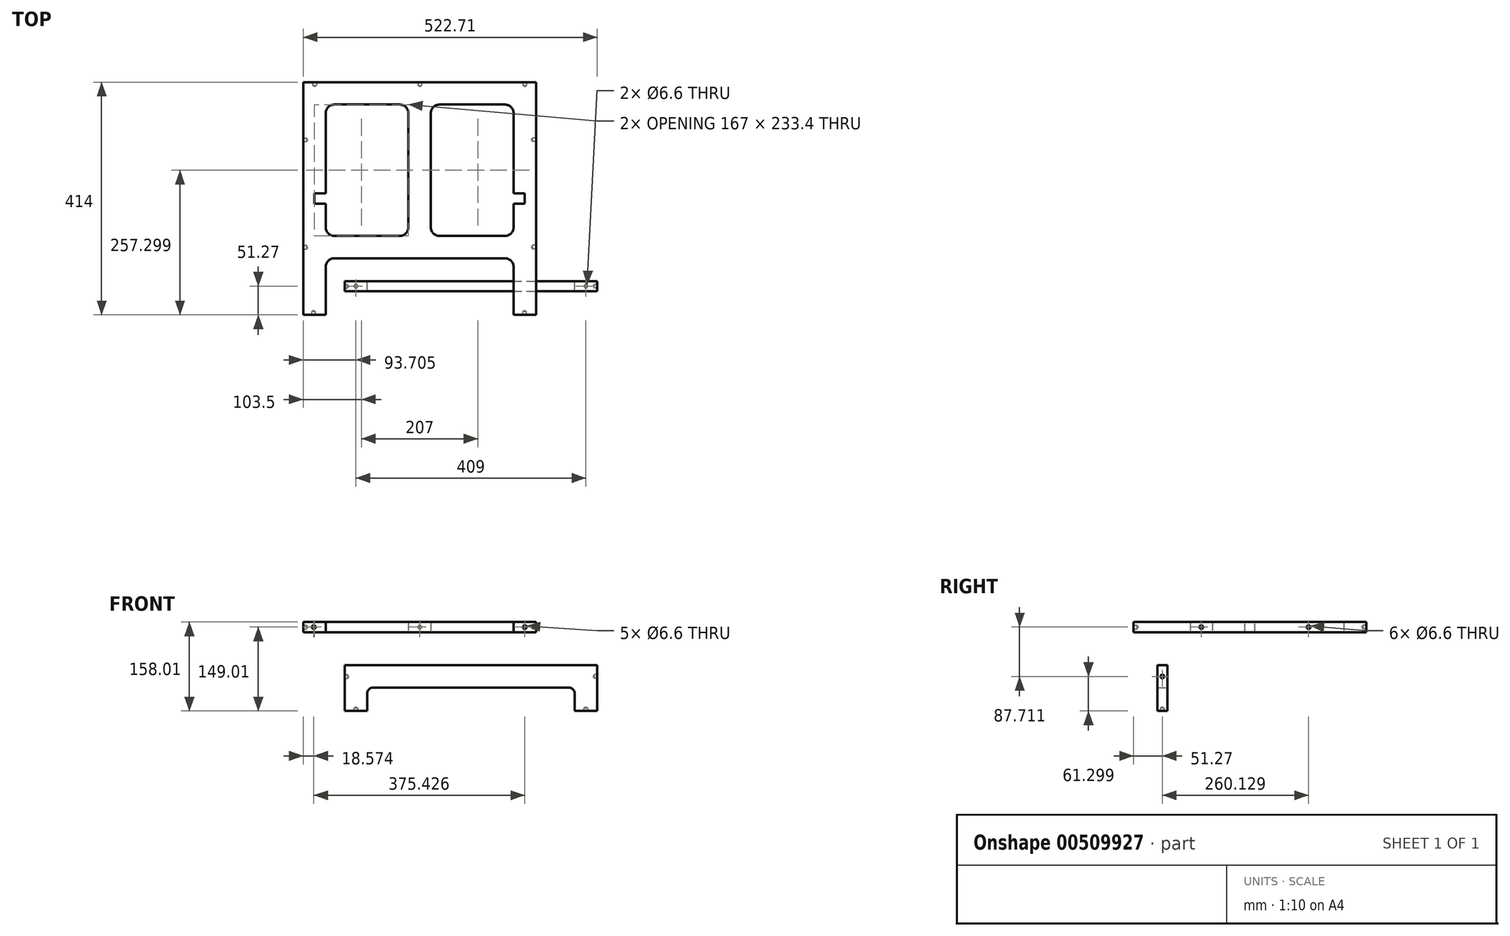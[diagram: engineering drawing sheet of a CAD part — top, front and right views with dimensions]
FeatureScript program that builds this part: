
annotation { "Feature Type Name" : "Feature", "Feature Type Description" : "" }
export const myFeature = defineFeature(function(context is Context, id is Id, definition is map)
    precondition{}
    {
        {
            var Q0;
            Q0=qCreatedBy(makeId("Top.planeOp"),FACE);
            var sketch = newSketch(context, id + "F0", { "sketchPlane" : qUnion([Q0])});
            skLineSegment(sketch, "E0.top", {"start": v(-192, 353.73) * mm, "end": v(222, 353.73) * mm});
            skLineSegment(sketch, "E0.left", {"start": v(-192, -60.27) * mm, "end": v(-192, 353.73) * mm});
            skLineSegment(sketch, "E0.right", {"start": v(222, -60.27) * mm, "end": v(222, 353.73) * mm});
            skLineSegment(sketch, "E1.top", {"start": v(-137, 40.33) * mm, "end": v(167, 40.33) * mm});
            skLineSegment(sketch, "E1.left", {"start": v(-152, -60.27) * mm, "end": v(-152, 25.33) * mm});
            skLineSegment(sketch, "E1.right", {"start": v(182, -60.27) * mm, "end": v(182, 25.33) * mm});
            skLineSegment(sketch, "E2.bottom", {"start": v(50, 313.73) * mm, "end": v(167, 313.73) * mm});
            skLineSegment(sketch, "E2.top", {"start": v(50, 80.33) * mm, "end": v(167, 80.33) * mm});
            skLineSegment(sketch, "E2.left", {"start": v(35, 298.73) * mm, "end": v(35, 95.33) * mm});
            skLineSegment(sketch, "E2.right", {"start": v(182, 298.73) * mm, "end": v(182, 95.33) * mm});
            skPoint(sketch, "E3.visualSharp", {"position": v(-157, 313.73) * mm});
            skPoint(sketch, "E4.visualSharp", {"position": v(0, 80.33) * mm});
            skPoint(sketch, "E5.visualSharp", {"position": v(-152, 98.33) * mm});
            skPoint(sketch, "E6.visualSharp", {"position": v(35, 313.73) * mm});
            skArc(sketch, "E6.filletArc", {"start": v(50, 313.73) * mm, "mid": v(39.4, 309.34) * mm, "end": v(35, 298.73) * mm});
            skPoint(sketch, "E7.visualSharp", {"position": v(182, 313.73) * mm});
            skArc(sketch, "E7.filletArc", {"start": v(182, 298.73) * mm, "mid": v(177.6, 309.34) * mm, "end": v(167, 313.73) * mm});
            skPoint(sketch, "E8.visualSharp", {"position": v(182, 80.33) * mm});
            skArc(sketch, "E8.filletArc", {"start": v(167, 80.33) * mm, "mid": v(177.6, 84.72) * mm, "end": v(182, 95.33) * mm});
            skPoint(sketch, "E9.visualSharp", {"position": v(35, 80.33) * mm});
            skArc(sketch, "E9.filletArc", {"start": v(35, 95.33) * mm, "mid": v(39.4, 84.72) * mm, "end": v(50, 80.33) * mm});
            skPoint(sketch, "E10.visualSharp", {"position": v(-152, 40.33) * mm});
            skArc(sketch, "E10.filletArc", {"start": v(-137, 40.33) * mm, "mid": v(-147.6, 35.94) * mm, "end": v(-152, 25.33) * mm});
            skPoint(sketch, "E11.visualSharp", {"position": v(182, 40.33) * mm});
            skArc(sketch, "E11.filletArc", {"start": v(182, 25.33) * mm, "mid": v(177.6, 35.94) * mm, "end": v(167, 40.33) * mm});
            skLineSegment(sketch, "E12", {"start": v(-192, -60.27) * mm, "end": v(-152, -60.27) * mm});
            skLineSegment(sketch, "E13", {"start": v(182, -60.27) * mm, "end": v(222, -60.27) * mm});
            skLineSegment(sketch, "E14", {"start": v(15, 353.73) * mm, "end": v(15, -60.27) * mm});
            skLineSegment(sketch, "E15.MirrorCS", {"start": v(-5, 298.73) * mm, "end": v(-5, 95.33) * mm});
            skArc(sketch, "E16.MirrorCS", {"start": v(-20, 313.73) * mm, "mid": v(-9.4, 309.34) * mm, "end": v(-5, 298.73) * mm});
            skLineSegment(sketch, "E17.MirrorCS", {"start": v(-20, 313.73) * mm, "end": v(-137, 313.73) * mm});
            skArc(sketch, "E18.MirrorCS", {"start": v(-152, 298.73) * mm, "mid": v(-147.6, 309.34) * mm, "end": v(-137, 313.73) * mm});
            skLineSegment(sketch, "E19.MirrorCS", {"start": v(-152, 298.73) * mm, "end": v(-152, 95.33) * mm});
            skArc(sketch, "E20.MirrorCS", {"start": v(-137, 80.33) * mm, "mid": v(-147.6, 84.72) * mm, "end": v(-152, 95.33) * mm});
            skLineSegment(sketch, "E21.MirrorCS", {"start": v(-20, 80.33) * mm, "end": v(-137, 80.33) * mm});
            skArc(sketch, "E22.MirrorCS", {"start": v(-5, 95.33) * mm, "mid": v(-9.4, 84.72) * mm, "end": v(-20, 80.33) * mm});
            skSolve(sketch);
        }
        {
            var Q0;
            Q0=makeQuery(id+"F0.imprint","IMPRINT",FACE,{"disambiguationData":[TD([[makeQuery(id+"F0.imprint","IMPRINT",EDGE,{"derivedFrom":sQuery(id+"F0.wireOp",EDGE,"E0.top")}),-1.0]])]});
            extrude(context, id + "F1", {"entities" : qUnion([Q0]), "depth" : 18 * mm, "offsetDistance" : 25 * mm});
        }
        {
            var Q0;
            Q0=makeQuery(id+"F1.opExtrude","SWEPT_FACE",FACE,{"disambiguationData":[OSD([sQuery(id+"F0.wireOp",EDGE,"E0.top")])]});
            var sketch = newSketch(context, id + "F2", { "sketchPlane" : qUnion([Q0])});
            skLineSegment(sketch, "E23", {"start": v(-222, 9) * mm, "end": v(192, 9) * mm});
            skPoint(sketch, "E24", {"position": v(-202, 9) * mm});
            skPoint(sketch, "E25", {"position": v(-15, 9) * mm});
            skPoint(sketch, "E26", {"position": v(172, 9) * mm});
            skSolve(sketch);
        }
        {
            var Q0;
            Q0=makeQuery(id+"F1.opExtrude","SWEPT_FACE",FACE,{"disambiguationData":[OSD([sQuery(id+"F0.wireOp",EDGE,"E13")])]});
            var sketch = newSketch(context, id + "F3", { "sketchPlane" : qUnion([Q0])});
            skLineSegment(sketch, "E27", {"start": v(222, 9) * mm, "end": v(-191.48, 9) * mm});
            skPoint(sketch, "E28", {"position": v(202, 9) * mm});
            skPoint(sketch, "E29", {"position": v(-173.43, 9) * mm});
            skSolve(sketch);
        }
        {
            var Q0;
            Q0=makeQuery(id+"F1.opExtrude","SWEPT_FACE",FACE,{"disambiguationData":[OSD([sQuery(id+"F0.wireOp",EDGE,"E0.right")])]});
            var sketch = newSketch(context, id + "F4", { "sketchPlane" : qUnion([Q0])});
            skLineSegment(sketch, "E30", {"start": v(-60.27, 9) * mm, "end": v(353.73, 9) * mm});
            skPoint(sketch, "E31", {"position": v(60.33, 9) * mm});
            skPoint(sketch, "E32", {"position": v(251.13, 9) * mm});
            skSolve(sketch);
        }
        {
            var Q0;
            Q0=makeQuery(id+"F1.opExtrude","SWEPT_FACE",FACE,{"disambiguationData":[OSD([sQuery(id+"F0.wireOp",EDGE,"E0.left")])]});
            var sketch = newSketch(context, id + "F5", { "sketchPlane" : qUnion([Q0])});
            skLineSegment(sketch, "E33", {"start": v(60.27, 9) * mm, "end": v(-353.73, 9) * mm});
            skPoint(sketch, "E34", {"position": v(-60.33, 9) * mm});
            skPoint(sketch, "E35", {"position": v(-251.13, 9) * mm});
            skSolve(sketch);
        }
        {
            var Q0;
            Q0=sQuery(id+"F3.wireOp",VERTEX,"E28");
            var Q1;
            Q1=sQuery(id+"F3.wireOp",VERTEX,"E29");
            var Q2;
            Q2=sQuery(id+"F5.wireOp",VERTEX,"E34");
            var Q3;
            Q3=sQuery(id+"F5.wireOp",VERTEX,"E35");
            var Q4;
            Q4=sQuery(id+"F2.wireOp",VERTEX,"E26");
            var Q5;
            Q5=sQuery(id+"F2.wireOp",VERTEX,"E25");
            var Q6;
            Q6=sQuery(id+"F2.wireOp",VERTEX,"E24");
            var Q7;
            Q7=sQuery(id+"F4.wireOp",VERTEX,"E31");
            var Q8;
            Q8=sQuery(id+"F4.wireOp",VERTEX,"E32");
            var Q9;
            Q9=makeQuery(id+"F1.opExtrude","SWEPT_BODY",BODY,{"disambiguationData":[OSD([sQuery(id+"F0.wireOp",EDGE,"E0.top"),sQuery(id+"F0.wireOp",EDGE,"E0.left"),sQuery(id+"F0.wireOp",EDGE,"E0.right"),sQuery(id+"F0.wireOp",EDGE,"E1.top"),sQuery(id+"F0.wireOp",EDGE,"E1.left"),sQuery(id+"F0.wireOp",EDGE,"E1.right"),sQuery(id+"F0.wireOp",EDGE,"E2.bottom"),sQuery(id+"F0.wireOp",EDGE,"E2.top"),sQuery(id+"F0.wireOp",EDGE,"E2.left"),sQuery(id+"F0.wireOp",EDGE,"E2.right"),sQuery(id+"F0.wireOp",EDGE,"E6.filletArc"),sQuery(id+"F0.wireOp",EDGE,"E7.filletArc"),sQuery(id+"F0.wireOp",EDGE,"E8.filletArc"),sQuery(id+"F0.wireOp",EDGE,"E9.filletArc"),sQuery(id+"F0.wireOp",EDGE,"E10.filletArc"),sQuery(id+"F0.wireOp",EDGE,"E11.filletArc"),sQuery(id+"F0.wireOp",EDGE,"E12"),sQuery(id+"F0.wireOp",EDGE,"E13"),sQuery(id+"F0.wireOp",EDGE,"E15.MirrorCS"),sQuery(id+"F0.wireOp",EDGE,"E16.MirrorCS"),sQuery(id+"F0.wireOp",EDGE,"E17.MirrorCS"),sQuery(id+"F0.wireOp",EDGE,"E18.MirrorCS"),sQuery(id+"F0.wireOp",EDGE,"E19.MirrorCS"),sQuery(id+"F0.wireOp",EDGE,"E20.MirrorCS"),sQuery(id+"F0.wireOp",EDGE,"E21.MirrorCS"),sQuery(id+"F0.wireOp",EDGE,"E22.MirrorCS")])]});
            hole(context, id + "F6", {"style" : HoleStyle.SIMPLE, "endStyle" : HoleEndStyle.BLIND, "standardTappedOrClearance" : lookupTablePath({ "standard" : "ISO", "fit" : "Normal", "size" : "M6", "type" : "Clearance" }), "standardBlindInLast" : lookupTablePath({ "fit" : "Standard", "standard" : "ISO", "size" : "M6", "type" : "Clearance" }), "holeDiameter" : 6.6 * mm, "holeDepth" : 6 * mm, "isTappedThrough" : true, "tappedDepth" : 12 * mm, "tapClearance" : 3, "locations" : qUnion([Q0, Q1, Q2, Q3, Q4, Q5, Q6, Q7, Q8]), "scope" : qUnion([Q9])});
        }
        {
            var Q0;
            Q0=makeQuery(id+"F1.opExtrude","SWEPT_BODY",BODY,{"disambiguationData":[OSD([sQuery(id+"F0.wireOp",EDGE,"E0.top"),sQuery(id+"F0.wireOp",EDGE,"E0.left"),sQuery(id+"F0.wireOp",EDGE,"E0.right"),sQuery(id+"F0.wireOp",EDGE,"E1.top"),sQuery(id+"F0.wireOp",EDGE,"E1.left"),sQuery(id+"F0.wireOp",EDGE,"E1.right"),sQuery(id+"F0.wireOp",EDGE,"E2.bottom"),sQuery(id+"F0.wireOp",EDGE,"E2.top"),sQuery(id+"F0.wireOp",EDGE,"E2.left"),sQuery(id+"F0.wireOp",EDGE,"E2.right"),sQuery(id+"F0.wireOp",EDGE,"E6.filletArc"),sQuery(id+"F0.wireOp",EDGE,"E7.filletArc"),sQuery(id+"F0.wireOp",EDGE,"E8.filletArc"),sQuery(id+"F0.wireOp",EDGE,"E9.filletArc"),sQuery(id+"F0.wireOp",EDGE,"E10.filletArc"),sQuery(id+"F0.wireOp",EDGE,"E11.filletArc"),sQuery(id+"F0.wireOp",EDGE,"E12"),sQuery(id+"F0.wireOp",EDGE,"E13"),sQuery(id+"F0.wireOp",EDGE,"E15.MirrorCS"),sQuery(id+"F0.wireOp",EDGE,"E16.MirrorCS"),sQuery(id+"F0.wireOp",EDGE,"E17.MirrorCS"),sQuery(id+"F0.wireOp",EDGE,"E18.MirrorCS"),sQuery(id+"F0.wireOp",EDGE,"E19.MirrorCS"),sQuery(id+"F0.wireOp",EDGE,"E20.MirrorCS"),sQuery(id+"F0.wireOp",EDGE,"E21.MirrorCS"),sQuery(id+"F0.wireOp",EDGE,"E22.MirrorCS")])]});
            var Q1;
            Q1=makeQuery(id+"F1.opExtrude","CAP_EDGE",EDGE,{"disambiguationData":[OSD([sQuery(id+"F0.wireOp",EDGE,"E0.top")])],"isStart":false});
            transform(context, id + "F7", {"entities" : qUnion([Q0]), "transformType" : TransformType.ROTATION, "transformAxis" : qUnion([Q1]), "angle" : 90 * degree, "makeCopy" : false});
        }
        {
            var Q0;
            Q0=makeQuery(id+"F1.opExtrude","SWEPT_BODY",BODY,{"disambiguationData":[OSD([sQuery(id+"F0.wireOp",EDGE,"E0.top"),sQuery(id+"F0.wireOp",EDGE,"E0.left"),sQuery(id+"F0.wireOp",EDGE,"E0.right"),sQuery(id+"F0.wireOp",EDGE,"E1.top"),sQuery(id+"F0.wireOp",EDGE,"E1.left"),sQuery(id+"F0.wireOp",EDGE,"E1.right"),sQuery(id+"F0.wireOp",EDGE,"E2.bottom"),sQuery(id+"F0.wireOp",EDGE,"E2.top"),sQuery(id+"F0.wireOp",EDGE,"E2.left"),sQuery(id+"F0.wireOp",EDGE,"E2.right"),sQuery(id+"F0.wireOp",EDGE,"E6.filletArc"),sQuery(id+"F0.wireOp",EDGE,"E7.filletArc"),sQuery(id+"F0.wireOp",EDGE,"E8.filletArc"),sQuery(id+"F0.wireOp",EDGE,"E9.filletArc"),sQuery(id+"F0.wireOp",EDGE,"E10.filletArc"),sQuery(id+"F0.wireOp",EDGE,"E11.filletArc"),sQuery(id+"F0.wireOp",EDGE,"E12"),sQuery(id+"F0.wireOp",EDGE,"E13"),sQuery(id+"F0.wireOp",EDGE,"E15.MirrorCS"),sQuery(id+"F0.wireOp",EDGE,"E16.MirrorCS"),sQuery(id+"F0.wireOp",EDGE,"E17.MirrorCS"),sQuery(id+"F0.wireOp",EDGE,"E18.MirrorCS"),sQuery(id+"F0.wireOp",EDGE,"E19.MirrorCS"),sQuery(id+"F0.wireOp",EDGE,"E20.MirrorCS"),sQuery(id+"F0.wireOp",EDGE,"E21.MirrorCS"),sQuery(id+"F0.wireOp",EDGE,"E22.MirrorCS")])]});
            var Q1;
            Q1=makeQuery(id+"F1.opExtrude","CAP_EDGE",EDGE,{"disambiguationData":[OSD([sQuery(id+"F0.wireOp",EDGE,"E0.top")])],"isStart":false});
            transform(context, id + "F8", {"entities" : qUnion([Q0]), "transformType" : TransformType.ROTATION, "transformAxis" : qUnion([Q1]), "angle" : 90 * degree, "oppositeDirection" : true, "makeCopy" : false});
        }
        {
            var Q0;
            Q0=makeQuery(id+"F1.opExtrude","CAP_FACE",FACE,{"disambiguationData":[OSD([sQuery(id+"F0.wireOp",EDGE,"E0.top"),sQuery(id+"F0.wireOp",EDGE,"E0.left"),sQuery(id+"F0.wireOp",EDGE,"E0.right"),sQuery(id+"F0.wireOp",EDGE,"E1.top"),sQuery(id+"F0.wireOp",EDGE,"E1.left"),sQuery(id+"F0.wireOp",EDGE,"E1.right"),sQuery(id+"F0.wireOp",EDGE,"E2.bottom"),sQuery(id+"F0.wireOp",EDGE,"E2.top"),sQuery(id+"F0.wireOp",EDGE,"E2.left"),sQuery(id+"F0.wireOp",EDGE,"E2.right"),sQuery(id+"F0.wireOp",EDGE,"E6.filletArc"),sQuery(id+"F0.wireOp",EDGE,"E7.filletArc"),sQuery(id+"F0.wireOp",EDGE,"E8.filletArc"),sQuery(id+"F0.wireOp",EDGE,"E9.filletArc"),sQuery(id+"F0.wireOp",EDGE,"E10.filletArc"),sQuery(id+"F0.wireOp",EDGE,"E11.filletArc"),sQuery(id+"F0.wireOp",EDGE,"E12"),sQuery(id+"F0.wireOp",EDGE,"E13"),sQuery(id+"F0.wireOp",EDGE,"E15.MirrorCS"),sQuery(id+"F0.wireOp",EDGE,"E16.MirrorCS"),sQuery(id+"F0.wireOp",EDGE,"E17.MirrorCS"),sQuery(id+"F0.wireOp",EDGE,"E18.MirrorCS"),sQuery(id+"F0.wireOp",EDGE,"E19.MirrorCS"),sQuery(id+"F0.wireOp",EDGE,"E20.MirrorCS"),sQuery(id+"F0.wireOp",EDGE,"E21.MirrorCS"),sQuery(id+"F0.wireOp",EDGE,"E22.MirrorCS")])],"isStart":false});
            var sketch = newSketch(context, id + "F9", { "sketchPlane" : qUnion([Q0])});
            skPoint(sketch, "E36", {"position": v(-192, 146.73) * mm});
            skPoint(sketch, "E37", {"position": v(222, 146.73) * mm});
            skPoint(sketch, "E38", {"position": v(-172, 146.73) * mm});
            skPoint(sketch, "E39", {"position": v(202, 146.73) * mm});
            skLineSegment(sketch, "E40", {"start": v(-172, 146.73) * mm, "end": v(-172, 155.73) * mm});
            skLineSegment(sketch, "E41", {"start": v(-172, 146.73) * mm, "end": v(-172, 137.73) * mm});
            skLineSegment(sketch, "E42", {"start": v(-172, 137.73) * mm, "end": v(-152, 137.73) * mm});
            skLineSegment(sketch, "E43", {"start": v(-172, 155.73) * mm, "end": v(-152, 155.73) * mm});
            skLineSegment(sketch, "E44", {"start": v(-152, 137.73) * mm, "end": v(-152, 155.73) * mm});
            skLineSegment(sketch, "E45", {"start": v(202, 146.73) * mm, "end": v(202, 155.73) * mm});
            skLineSegment(sketch, "E46", {"start": v(202, 146.73) * mm, "end": v(202, 137.73) * mm});
            skLineSegment(sketch, "E47", {"start": v(202, 137.73) * mm, "end": v(182, 137.73) * mm});
            skLineSegment(sketch, "E48", {"start": v(182, 137.73) * mm, "end": v(182, 155.73) * mm});
            skLineSegment(sketch, "E49", {"start": v(182, 155.73) * mm, "end": v(202, 155.73) * mm});
            skSolve(sketch);
        }
        {
            var Q0;
            Q0=makeQuery(id+"F9.imprint","IMPRINT",FACE,{"disambiguationData":[TD([[makeQuery(id+"F9.imprint","IMPRINT",EDGE,{"derivedFrom":sQuery(id+"F9.wireOp",EDGE,"E40")}),-1.0]])]});
            var Q1;
            Q1=makeQuery(id+"F9.imprint","IMPRINT",FACE,{"disambiguationData":[TD([[makeQuery(id+"F9.imprint","IMPRINT",EDGE,{"derivedFrom":sQuery(id+"F9.wireOp",EDGE,"E45")}),1.0]])]});
            extrude(context, id + "F10", {"entities" : qUnion([Q0, Q1]), "operationType" : NewBodyOperationType.REMOVE, "oppositeDirection" : true, "depth" : 18 * mm, "offsetDistance" : 25 * mm});
        }
        {
            var Q0;
            Q0=qCreatedBy(makeId("Front.planeOp"),FACE);
            var sketch = newSketch(context, id + "F11", { "sketchPlane" : qUnion([Q0])});
            skLineSegment(sketch, "E50.left", {"start": v(330.7, -58.71) * mm, "end": v(330.7, -140.01) * mm});
            skLineSegment(sketch, "E50.right", {"start": v(-118.3, -58.71) * mm, "end": v(-118.3, -140.01) * mm});
            skLineSegment(sketch, "E51", {"start": v(290.7, -140.01) * mm, "end": v(290.7, -108.71) * mm});
            skLineSegment(sketch, "E52", {"start": v(280.7, -98.71) * mm, "end": v(-68.3, -98.71) * mm});
            skLineSegment(sketch, "E53", {"start": v(-78.3, -108.71) * mm, "end": v(-78.3, -140.01) * mm});
            skLineSegment(sketch, "E54", {"start": v(290.7, -140.01) * mm, "end": v(330.7, -140.01) * mm});
            skLineSegment(sketch, "E55", {"start": v(-78.3, -140.01) * mm, "end": v(-118.3, -140.01) * mm});
            skLineSegment(sketch, "E56", {"start": v(-118.3, -58.71) * mm, "end": v(330.7, -58.71) * mm});
            skPoint(sketch, "E57.visualSharp", {"position": v(-78.3, -98.71) * mm});
            skArc(sketch, "E57.filletArc", {"start": v(-68.3, -98.71) * mm, "mid": v(-75.37, -101.64) * mm, "end": v(-78.3, -108.71) * mm});
            skPoint(sketch, "E58.visualSharp", {"position": v(290.7, -98.71) * mm});
            skArc(sketch, "E58.filletArc", {"start": v(290.7, -108.71) * mm, "mid": v(287.78, -101.64) * mm, "end": v(280.7, -98.71) * mm});
            skSolve(sketch);
        }
        {
            var Q0;
            Q0=makeQuery(id+"F11.imprint","IMPRINT",FACE,{"disambiguationData":[TD([[makeQuery(id+"F11.imprint","IMPRINT",EDGE,{"derivedFrom":sQuery(id+"F11.wireOp",EDGE,"E50.left")}),-1.0]])]});
            extrude(context, id + "F12", {"entities" : qUnion([Q0]), "depth" : 18 * mm, "offsetDistance" : 25 * mm});
        }
        {
            var Q0;
            Q0=makeQuery(id+"F12.opExtrude","SWEPT_FACE",FACE,{"disambiguationData":[OSD([sQuery(id+"F11.wireOp",EDGE,"E55")])]});
            var sketch = newSketch(context, id + "F13", { "sketchPlane" : qUnion([Q0])});
            skLineSegment(sketch, "E59", {"start": v(-118.3, 9) * mm, "end": v(-78.3, 9) * mm});
            skPoint(sketch, "E60", {"position": v(-98.3, 9) * mm});
            skSolve(sketch);
        }
        {
            var Q0;
            Q0=makeQuery(id+"F12.opExtrude","SWEPT_FACE",FACE,{"disambiguationData":[OSD([sQuery(id+"F11.wireOp",EDGE,"E54")])]});
            var sketch = newSketch(context, id + "F14", { "sketchPlane" : qUnion([Q0])});
            skLineSegment(sketch, "E61", {"start": v(290.7, 9) * mm, "end": v(330.7, 9) * mm});
            skPoint(sketch, "E62", {"position": v(310.7, 9) * mm});
            skSolve(sketch);
        }
        {
            var Q0;
            Q0=makeQuery(id+"F12.opExtrude","SWEPT_FACE",FACE,{"disambiguationData":[OSD([sQuery(id+"F11.wireOp",EDGE,"E50.right")])]});
            var sketch = newSketch(context, id + "F15", { "sketchPlane" : qUnion([Q0])});
            skLineSegment(sketch, "E63", {"start": v(9, -58.71) * mm, "end": v(9, -140.01) * mm});
            skPoint(sketch, "E64", {"position": v(9, -78.71) * mm});
            skSolve(sketch);
        }
        {
            var Q0;
            Q0=makeQuery(id+"F12.opExtrude","SWEPT_FACE",FACE,{"disambiguationData":[OSD([sQuery(id+"F11.wireOp",EDGE,"E50.left")])]});
            var sketch = newSketch(context, id + "F16", { "sketchPlane" : qUnion([Q0])});
            skLineSegment(sketch, "E65", {"start": v(-9, -58.71) * mm, "end": v(-9, -140.01) * mm});
            skPoint(sketch, "E66", {"position": v(-9, -78.71) * mm});
            skSolve(sketch);
        }
        {
            var Q0;
            Q0=sQuery(id+"F13.wireOp",VERTEX,"E60");
            var Q1;
            Q1=sQuery(id+"F15.wireOp",VERTEX,"E64");
            var Q2;
            Q2=sQuery(id+"F16.wireOp",VERTEX,"E66");
            var Q3;
            Q3=sQuery(id+"F14.wireOp",VERTEX,"E62");
            var Q4;
            Q4=makeQuery(id+"F12.opExtrude","SWEPT_BODY",BODY,{"disambiguationData":[OSD([sQuery(id+"F11.wireOp",EDGE,"E50.left"),sQuery(id+"F11.wireOp",EDGE,"E50.right"),sQuery(id+"F11.wireOp",EDGE,"E51"),sQuery(id+"F11.wireOp",EDGE,"E52"),sQuery(id+"F11.wireOp",EDGE,"E53"),sQuery(id+"F11.wireOp",EDGE,"E54"),sQuery(id+"F11.wireOp",EDGE,"E55"),sQuery(id+"F11.wireOp",EDGE,"E56"),sQuery(id+"F11.wireOp",EDGE,"E57.filletArc"),sQuery(id+"F11.wireOp",EDGE,"E58.filletArc")])]});
            hole(context, id + "F17", {"style" : HoleStyle.SIMPLE, "endStyle" : HoleEndStyle.BLIND, "standardTappedOrClearance" : lookupTablePath({ "fit" : "Normal", "standard" : "ISO", "size" : "M6", "type" : "Clearance" }), "standardBlindInLast" : lookupTablePath({ "fit" : "Standard", "standard" : "ISO", "size" : "M6", "type" : "Clearance" }), "holeDiameter" : 6.6 * mm, "holeDepth" : 5 * mm, "isTappedThrough" : true, "tappedDepth" : 12 * mm, "tapClearance" : 3, "locations" : qUnion([Q0, Q1, Q2, Q3]), "scope" : qUnion([Q4])});
        }
    });
